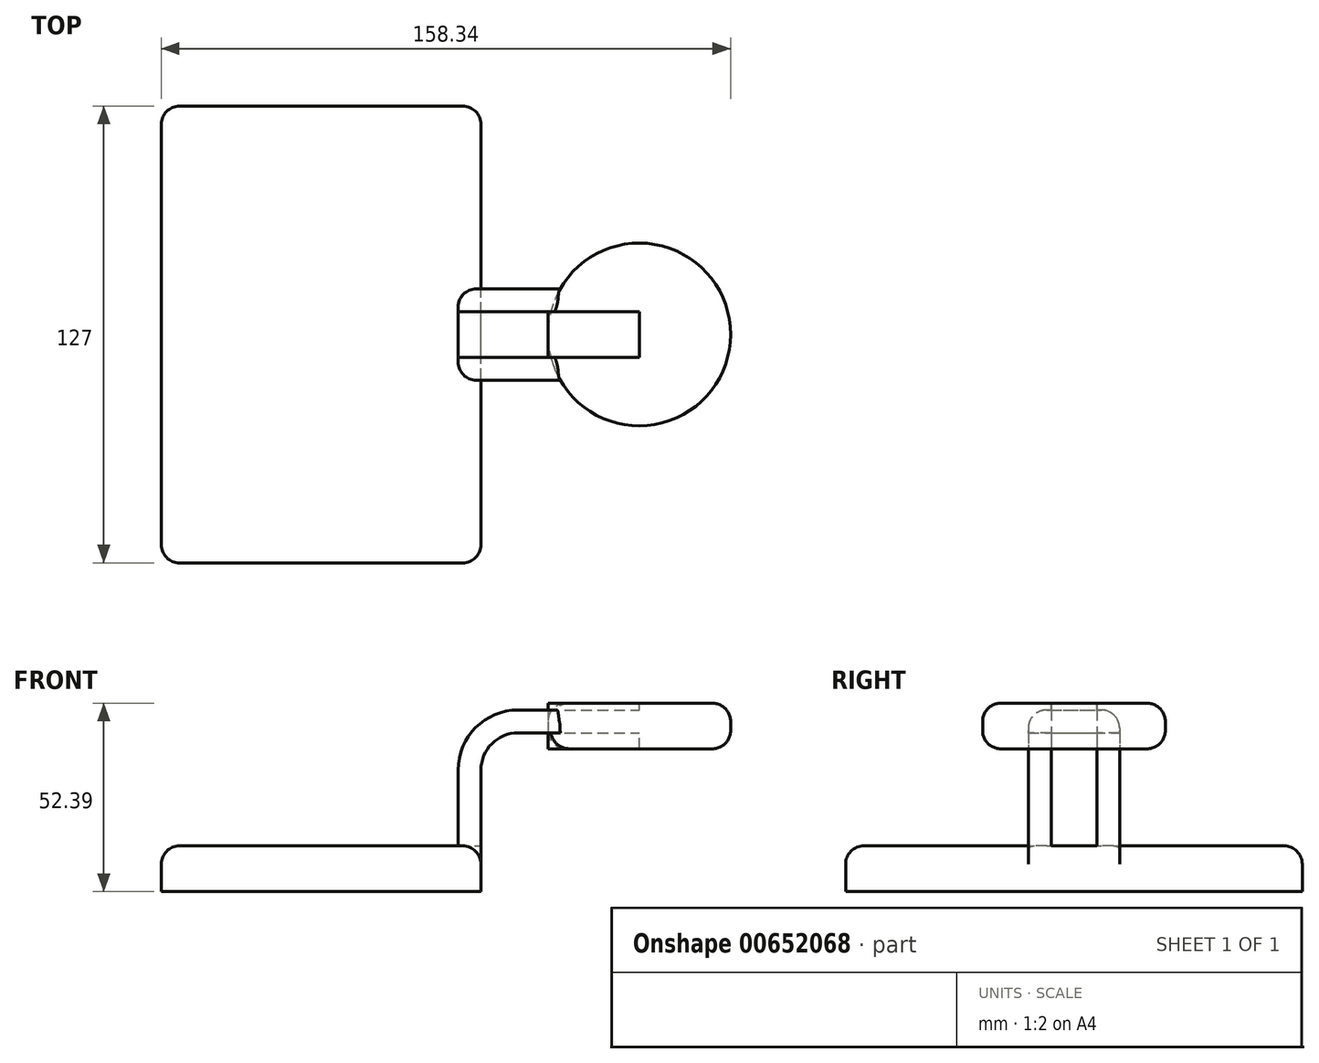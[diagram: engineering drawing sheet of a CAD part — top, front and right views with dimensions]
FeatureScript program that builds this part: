
annotation { "Feature Type Name" : "Feature", "Feature Type Description" : "" }
export const myFeature = defineFeature(function(context is Context, id is Id, definition is map)
    precondition{}
    {
        {
            var Q0;
            Q0=qCreatedBy(makeId("Front.planeOp"),FACE);
            var sketch = newSketch(context, id + "F0", { "sketchPlane" : qUnion([Q0])});
            skLineSegment(sketch, "E0.bottom", {"start": v(-93.09, -15.68) * mm, "end": v(-4.19, -15.68) * mm});
            skLineSegment(sketch, "E0.top", {"start": v(-93.09, -28.38) * mm, "end": v(-4.19, -28.38) * mm});
            skLineSegment(sketch, "E0.left", {"start": v(-93.09, -15.68) * mm, "end": v(-93.09, -28.38) * mm});
            skLineSegment(sketch, "E0.right", {"start": v(-4.19, -15.68) * mm, "end": v(-4.19, -28.38) * mm});
            skLineSegment(sketch, "E1.bottom", {"start": v(14.45, 24.01) * mm, "end": v(65.25, 24.01) * mm});
            skLineSegment(sketch, "E1.top", {"start": v(14.45, 11.31) * mm, "end": v(65.25, 11.31) * mm});
            skLineSegment(sketch, "E1.left", {"start": v(14.45, 24.01) * mm, "end": v(14.45, 11.31) * mm});
            skLineSegment(sketch, "E1.right", {"start": v(65.25, 24.01) * mm, "end": v(65.25, 11.31) * mm});
            skLineSegment(sketch, "E2", {"start": v(-4.19, -15.68) * mm, "end": v(-4.19, 5.43) * mm});
            skArc(sketch, "E3", {"start": v(-4.19, 5.43) * mm, "mid": v(-1.16, 12.74) * mm, "end": v(6.15, 15.77) * mm});
            skLineSegment(sketch, "E4", {"start": v(6.15, 15.77) * mm, "end": v(39.85, 15.77) * mm});
            skLineSegment(sketch, "E5.0", {"start": v(6.15, 22.12) * mm, "end": v(39.85, 22.12) * mm});
            skArc(sketch, "E5.1", {"start": v(-10.54, 5.43) * mm, "mid": v(-5.65, 17.23) * mm, "end": v(6.15, 22.12) * mm});
            skLineSegment(sketch, "E5.2", {"start": v(-10.54, -8.53) * mm, "end": v(-10.54, 5.43) * mm});
            skLineSegment(sketch, "E6", {"start": v(39.85, 15.77) * mm, "end": v(39.85, 22.12) * mm});
            skLineSegment(sketch, "E7", {"start": v(-10.54, -8.53) * mm, "end": v(-10.54, -15.68) * mm});
            skFitSpline(sketch, "E8", {"points": [v(-93.09, -15.68) * mm, v(14.45, 24.01) * mm], "startDerivative": vector(86.93, 67.96) * mm, "endDerivative": vector(124.05, 1.82) * mm});
            skLineSegment(sketch, "E9", {"start": v(39.85, 11.31) * mm, "end": v(39.85, 24.01) * mm});
            skSolve(sketch);
        }
        {
            var Q0;
            Q0=makeQuery(id+"F0.imprint","IMPRINT",FACE,{"disambiguationData":[TD([[makeQuery(id+"F0.imprint","IMPRINT",EDGE,{"derivedFrom":sQuery(id+"F0.wireOp",EDGE,"E0.top")}),1.0]])]});
            extrude(context, id + "F1", {"entities" : qUnion([Q0]), "endBound" : BoundingType.SYMMETRIC, "depth" : 127 * mm, "offsetDistance" : 25.4 * mm});
        }
        {
            var Q0;
            {var subQ1=sQuery(id+"F0.wireOp",EDGE,"E2");Q0=makeQuery(id+"F0.imprint","IMPRINT",FACE,{"disambiguationData":[TD([[makeQuery(id+"F0.imprint","IMPRINT",EDGE,{"derivedFrom":subQ1}),1.0]])]});}
            var Q1;
            {var subQ0=sQuery(id+"F0.wireOp",EDGE,"E4");var subQ1=sQuery(id+"F0.wireOp",EDGE,"E1.left");var subQ2=makeQuery(id+"F0.imprint","INTERSECT",VERTEX,{"derivedFrom":[subQ1,subQ0]});Q1=makeQuery(id+"F0.imprint","IMPRINT",FACE,{"disambiguationData":[TD([[makeQuery(id+"F0.imprint","IMPRINT",EDGE,{"disambiguationData":[TD([[subQ2,1.0]])],"derivedFrom":subQ1}),1.0]])]});}
            extrude(context, id + "F2", {"entities" : qUnion([Q0, Q1]), "operationType" : NewBodyOperationType.ADD, "endBound" : BoundingType.SYMMETRIC, "depth" : 25.4 * mm, "offsetDistance" : 25.4 * mm});
        }
        {
            var Q0;
            {var subQ0=sQuery(id+"F0.wireOp",EDGE,"E5.1");Q0=makeQuery(id+"F0.imprint","IMPRINT",FACE,{"disambiguationData":[TD([[makeQuery(id+"F0.imprint","IMPRINT",EDGE,{"derivedFrom":subQ0}),1.0]])]});}
            var Q1;
            {var subQ0=sQuery(id+"F0.wireOp",EDGE,"E1.left");var subQ1=sQuery(id+"F0.wireOp",EDGE,"E1.top");var subQ2=makeQuery(id+"F0.imprint","INTERSECT",VERTEX,{"derivedFrom":[subQ1,subQ0]});Q1=makeQuery(id+"F0.imprint","IMPRINT",FACE,{"disambiguationData":[TD([[makeQuery(id+"F0.imprint","IMPRINT",EDGE,{"disambiguationData":[TD([[subQ2,-1.0]])],"derivedFrom":subQ1}),1.0]])]});}
            var Q2;
            {var subQ3=sQuery(id+"F0.wireOp",EDGE,"E9");var subQ5=sQuery(id+"F0.wireOp",EDGE,"E5.0");var subQ6=makeQuery(id+"F0.imprint","INTERSECT",VERTEX,{"derivedFrom":[subQ5,subQ3]});Q2=makeQuery(id+"F0.imprint","IMPRINT",FACE,{"disambiguationData":[TD([[makeQuery(id+"F0.imprint","IMPRINT",EDGE,{"disambiguationData":[TD([[subQ6,1.0]])],"derivedFrom":subQ5}),1.0]])]});}
            extrude(context, id + "F3", {"entities" : qUnion([Q0, Q1, Q2]), "endBound" : BoundingType.SYMMETRIC, "depth" : 12.7 * mm, "offsetDistance" : 25.4 * mm});
        }
        {
            var Q0;
            {var subQ0=sQuery(id+"F0.wireOp",EDGE,"E1.right");Q0=makeQuery(id+"F0.imprint","IMPRINT",FACE,{"disambiguationData":[TD([[makeQuery(id+"F0.imprint","IMPRINT",EDGE,{"derivedFrom":subQ0}),-1.0]])]});}
            var Q1;
            Q1=sQuery(id+"F0.wireOp",EDGE,"E9");
            revolve(context, id + "F4", {"entities" : qUnion([Q0]), "axis" : qUnion([Q1]), "revolveType" : RevolveType.FULL});
        }
        {
            var Q0;
            Q0=makeQuery(id+"F1.opExtrude","CAP_EDGE",EDGE,{"disambiguationData":[OSD([sQuery(id+"F0.wireOp",EDGE,"E0.right")])],"isStart":false});
            var Q1;
            Q1=makeQuery(id+"F1.opExtrude","CAP_EDGE",EDGE,{"disambiguationData":[OSD([sQuery(id+"F0.wireOp",EDGE,"E0.left")])],"isStart":false});
            var Q2;
            Q2=makeQuery(id+"F1.opExtrude","CAP_EDGE",EDGE,{"disambiguationData":[OSD([sQuery(id+"F0.wireOp",EDGE,"E0.right")])],"isStart":true});
            var Q3;
            Q3=makeQuery(id+"F1.opExtrude","CAP_EDGE",EDGE,{"disambiguationData":[OSD([sQuery(id+"F0.wireOp",EDGE,"E0.left")])],"isStart":true});
            var Q4;
            Q4=makeQuery(id+"F3.opExtrude","CAP_EDGE",EDGE,{"disambiguationData":[OSD([sQuery(id+"F0.wireOp",EDGE,"E8")])],"isStart":false});
            var Q5;
            Q5=makeQuery(id+"F3.opExtrude","CAP_EDGE",EDGE,{"disambiguationData":[OSD([sQuery(id+"F0.wireOp",EDGE,"E8")])],"isStart":true});
            var Q6;
            Q6=makeQuery(id+"F1.opExtrude","SWEPT_EDGE",EDGE,{"disambiguationData":[OSD([sQuery(id+"F0.wireOp",EDGE,"E0.bottom"),sQuery(id+"F0.wireOp",EDGE,"E0.left"),sQuery(id+"F0.wireOp",EDGE,"E8")])]});
            var Q7;
            Q7=makeQuery(id+"F1.opExtrude","CAP_EDGE",EDGE,{"disambiguationData":[OSD([sQuery(id+"F0.wireOp",EDGE,"E0.bottom")])],"isStart":false});
            var Q8;
            {var subQ0=sQuery(id+"F0.wireOp",EDGE,"E2");var subQ1=sQuery(id+"F0.wireOp",EDGE,"E0.bottom");var subQ2=sQuery(id+"F0.wireOp",EDGE,"E0.right");Q8=makeQuery(id+"F2.boolean.opBoolean","SPLIT",EDGE,{"disambiguationData":[TD([makeQuery(id+"F1.opExtrude","CAP_FACE",FACE,{"disambiguationData":[OSD([subQ1,sQuery(id+"F0.wireOp",EDGE,"E0.top"),sQuery(id+"F0.wireOp",EDGE,"E0.left"),subQ2])],"isStart":false})])],"derivedFrom":makeQuery(id+"F1.opExtrude","SWEPT_EDGE",EDGE,{"disambiguationData":[OSD([subQ1,subQ2,subQ0])]})});}
            var Q9;
            Q9=makeQuery(id+"F1.opExtrude","CAP_EDGE",EDGE,{"disambiguationData":[OSD([sQuery(id+"F0.wireOp",EDGE,"E0.bottom")])],"isStart":true});
            var Q10;
            {var subQ0=sQuery(id+"F0.wireOp",EDGE,"E2");var subQ1=sQuery(id+"F0.wireOp",EDGE,"E0.bottom");var subQ2=sQuery(id+"F0.wireOp",EDGE,"E0.right");Q10=makeQuery(id+"F2.boolean.opBoolean","SPLIT",EDGE,{"disambiguationData":[TD([makeQuery(id+"F1.opExtrude","CAP_FACE",FACE,{"disambiguationData":[OSD([subQ1,sQuery(id+"F0.wireOp",EDGE,"E0.top"),sQuery(id+"F0.wireOp",EDGE,"E0.left"),subQ2])],"isStart":true})])],"derivedFrom":makeQuery(id+"F1.opExtrude","SWEPT_EDGE",EDGE,{"disambiguationData":[OSD([subQ1,subQ2,subQ0])]})});}
            fillet(context, id + "F5", {"entities" : qUnion([Q0, Q1, Q2, Q3, Q4, Q5, Q6, Q7, Q8, Q9, Q10]), "radius" : 5.08 * mm, "tangentPropagation" : true, "allowEdgeOverflow" : false});
        }
        {
            var Q0;
            Q0=makeQuery(id+"F4.opRevolve","SWEPT_EDGE",EDGE,{"disambiguationData":[OSD([sQuery(id+"F0.wireOp",EDGE,"E1.bottom"),sQuery(id+"F0.wireOp",EDGE,"E1.right")])]});
            fillet(context, id + "F6", {"entities" : qUnion([Q0]), "radius" : 5.08 * mm, "tangentPropagation" : true, "allowEdgeOverflow" : false});
        }
        {
            var Q0;
            Q0=makeQuery(id+"F2.opExtrude","CAP_EDGE",EDGE,{"disambiguationData":[OSD([sQuery(id+"F0.wireOp",EDGE,"E5.2"),sQuery(id+"F0.wireOp",EDGE,"E7")])],"isStart":true});
            var Q1;
            Q1=makeQuery(id+"F2.opExtrude","CAP_EDGE",EDGE,{"disambiguationData":[OSD([sQuery(id+"F0.wireOp",EDGE,"E5.2"),sQuery(id+"F0.wireOp",EDGE,"E7")])],"isStart":false});
            var Q2;
            Q2=makeQuery(id+"F4.opRevolve","SWEPT_EDGE",EDGE,{"disambiguationData":[OSD([sQuery(id+"F0.wireOp",EDGE,"E1.top"),sQuery(id+"F0.wireOp",EDGE,"E1.right")])]});
            fillet(context, id + "F7", {"entities" : qUnion([Q0, Q1, Q2]), "radius" : 5.08 * mm, "tangentPropagation" : true, "allowEdgeOverflow" : false});
        }
    });
